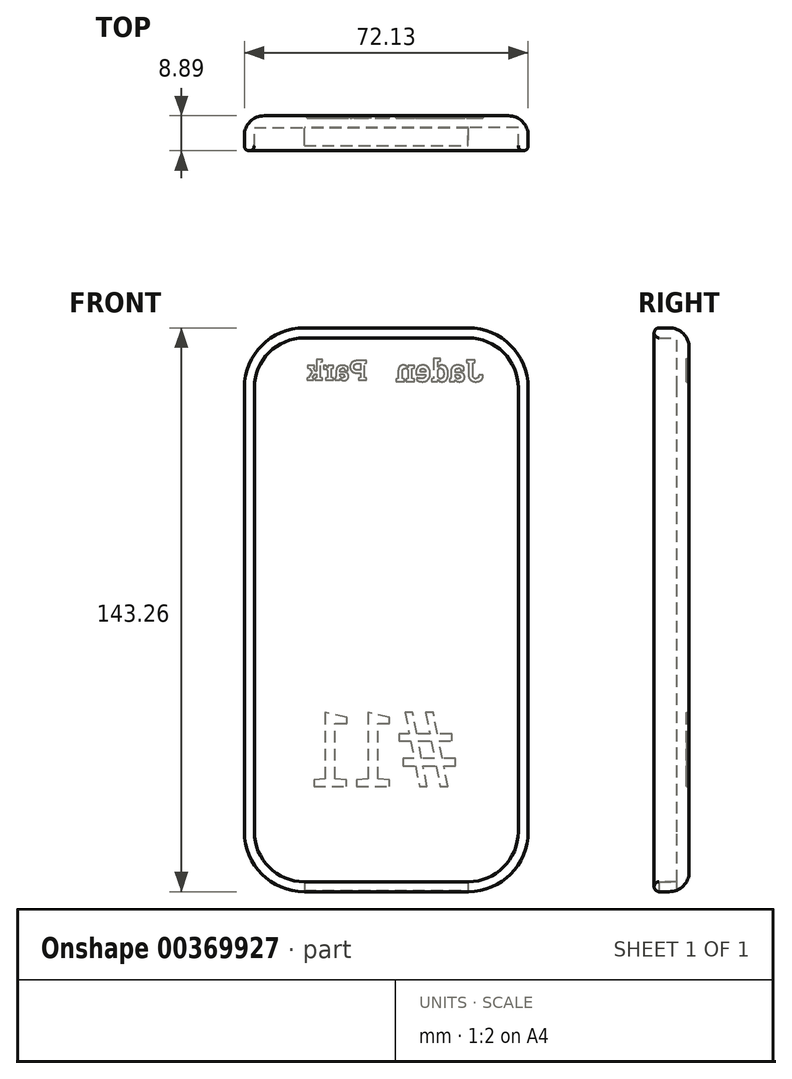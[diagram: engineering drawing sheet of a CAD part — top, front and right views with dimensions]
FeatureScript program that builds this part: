
annotation { "Feature Type Name" : "Feature", "Feature Type Description" : "" }
export const myFeature = defineFeature(function(context is Context, id is Id, definition is map)
    precondition{}
    {
        {
            var Q0;
            Q0=qCreatedBy(makeId("Front.planeOp"),FACE);
            var sketch = newSketch(context, id + "F0", { "sketchPlane" : qUnion([Q0])});
            skLineSegment(sketch, "E0.bottom", {"start": v(-22.84, 81.8) * mm, "end": v(18.81, 81.8) * mm});
            skLineSegment(sketch, "E0.top", {"start": v(-22.84, -56.38) * mm, "end": v(18.81, -56.38) * mm});
            skLineSegment(sketch, "E0.left", {"start": v(-35.54, 69.1) * mm, "end": v(-35.54, -43.68) * mm});
            skLineSegment(sketch, "E0.right", {"start": v(31.51, 69.1) * mm, "end": v(31.51, -43.68) * mm});
            skPoint(sketch, "E1.visualSharp", {"position": v(-35.54, 81.8) * mm});
            skArc(sketch, "E1.filletArc", {"start": v(-22.84, 81.8) * mm, "mid": v(-31.82, 78.08) * mm, "end": v(-35.54, 69.1) * mm});
            skPoint(sketch, "E2.visualSharp", {"position": v(31.51, 81.8) * mm});
            skArc(sketch, "E2.filletArc", {"start": v(31.51, 69.1) * mm, "mid": v(27.8, 78.08) * mm, "end": v(18.81, 81.8) * mm});
            skPoint(sketch, "E3.visualSharp", {"position": v(31.51, -56.38) * mm});
            skArc(sketch, "E3.filletArc", {"start": v(18.81, -56.38) * mm, "mid": v(27.8, -52.66) * mm, "end": v(31.51, -43.68) * mm});
            skPoint(sketch, "E4.visualSharp", {"position": v(-35.54, -56.38) * mm});
            skArc(sketch, "E4.filletArc", {"start": v(-35.54, -43.68) * mm, "mid": v(-31.82, -52.66) * mm, "end": v(-22.84, -56.38) * mm});
            skLineSegment(sketch, "E5.0", {"start": v(-22.84, 84.34) * mm, "end": v(18.81, 84.34) * mm});
            skArc(sketch, "E6.0", {"start": v(34.05, 69.1) * mm, "mid": v(29.6, 79.88) * mm, "end": v(18.81, 84.34) * mm});
            skArc(sketch, "E7.2", {"start": v(-22.84, 84.34) * mm, "mid": v(-33.62, 79.88) * mm, "end": v(-38.08, 69.1) * mm});
            skLineSegment(sketch, "E7.3", {"start": v(34.05, 69.1) * mm, "end": v(34.05, -43.68) * mm});
            skLineSegment(sketch, "E7.4", {"start": v(-38.08, 69.1) * mm, "end": v(-38.08, -43.68) * mm});
            skArc(sketch, "E7.5", {"start": v(-38.08, -43.68) * mm, "mid": v(-33.62, -54.45) * mm, "end": v(-22.84, -58.92) * mm});
            skLineSegment(sketch, "E7.6", {"start": v(-22.84, -58.92) * mm, "end": v(18.81, -58.92) * mm});
            skArc(sketch, "E7.7", {"start": v(18.81, -58.92) * mm, "mid": v(29.6, -54.45) * mm, "end": v(34.05, -43.68) * mm});
            skSolve(sketch);
        }
        {
            var Q0;
            Q0 = qSketchRegion(id + "F0", true);
            var Q1;
            Q1=makeQuery(id+"F0.imprint","IMPRINT",FACE,{"disambiguationData":[TD([[makeQuery(id+"F0.imprint","IMPRINT",EDGE,{"derivedFrom":sQuery(id+"F0.wireOp",EDGE,"E0.bottom")}),-1.0]])]});
            extrude(context, id + "F1", {"entities" : qUnion([Q0, Q1]), "depth" : 3.05 * mm});
        }
        {
            var Q0;
            Q0=makeQuery(id+"F0.imprint","IMPRINT",FACE,{"disambiguationData":[TD([[makeQuery(id+"F0.imprint","IMPRINT",EDGE,{"derivedFrom":sQuery(id+"F0.wireOp",EDGE,"E0.bottom")}),1.0]])]});
            extrude(context, id + "F2", {"entities" : qUnion([Q0]), "operationType" : NewBodyOperationType.ADD, "depth" : 8.9 * mm});
        }
        {
            var Q0;
            Q0=makeQuery(id+"F2.opExtrude","CAP_EDGE",EDGE,{"disambiguationData":[OSD([sQuery(id+"F0.wireOp",EDGE,"E1.filletArc")])],"isStart":false});
            var Q1;
            Q1=makeQuery(id+"F2.opExtrude","CAP_EDGE",EDGE,{"disambiguationData":[OSD([sQuery(id+"F0.wireOp",EDGE,"E0.bottom")])],"isStart":false});
            var Q2;
            Q2=makeQuery(id+"F2.opExtrude","CAP_EDGE",EDGE,{"disambiguationData":[OSD([sQuery(id+"F0.wireOp",EDGE,"E2.filletArc")])],"isStart":false});
            var Q3;
            Q3=makeQuery(id+"F2.opExtrude","CAP_EDGE",EDGE,{"disambiguationData":[OSD([sQuery(id+"F0.wireOp",EDGE,"E0.right")])],"isStart":false});
            var Q4;
            Q4=makeQuery(id+"F2.opExtrude","CAP_EDGE",EDGE,{"disambiguationData":[OSD([sQuery(id+"F0.wireOp",EDGE,"E3.filletArc")])],"isStart":false});
            var Q5;
            Q5=makeQuery(id+"F2.opExtrude","CAP_EDGE",EDGE,{"disambiguationData":[OSD([sQuery(id+"F0.wireOp",EDGE,"E4.filletArc")])],"isStart":false});
            var Q6;
            Q6=makeQuery(id+"F2.opExtrude","CAP_EDGE",EDGE,{"disambiguationData":[OSD([sQuery(id+"F0.wireOp",EDGE,"E7.3")])],"isStart":false});
            var Q7;
            Q7=makeQuery(id+"F2.opExtrude","CAP_EDGE",EDGE,{"disambiguationData":[OSD([sQuery(id+"F0.wireOp",EDGE,"E6.0")])],"isStart":false});
            var Q8;
            Q8=makeQuery(id+"F2.opExtrude","CAP_EDGE",EDGE,{"disambiguationData":[OSD([sQuery(id+"F0.wireOp",EDGE,"E5.0")])],"isStart":false});
            var Q9;
            Q9=makeQuery(id+"F2.opExtrude","CAP_EDGE",EDGE,{"disambiguationData":[OSD([sQuery(id+"F0.wireOp",EDGE,"E7.2")])],"isStart":false});
            var Q10;
            Q10=makeQuery(id+"F2.opExtrude","CAP_EDGE",EDGE,{"disambiguationData":[OSD([sQuery(id+"F0.wireOp",EDGE,"E7.5")])],"isStart":false});
            var Q11;
            Q11=makeQuery(id+"F2.opExtrude","CAP_EDGE",EDGE,{"disambiguationData":[OSD([sQuery(id+"F0.wireOp",EDGE,"E7.7")])],"isStart":false});
            var Q12;
            Q12=makeQuery(id+"F2.opExtrude","CAP_EDGE",EDGE,{"disambiguationData":[OSD([sQuery(id+"F0.wireOp",EDGE,"E0.left")])],"isStart":false});
            var Q13;
            Q13=makeQuery(id+"F2.opExtrude","CAP_EDGE",EDGE,{"disambiguationData":[OSD([sQuery(id+"F0.wireOp",EDGE,"E7.4")])],"isStart":false});
            fillet(context, id + "F3", {"entities" : qUnion([Q0, Q1, Q2, Q3, Q4, Q5, Q6, Q7, Q8, Q9, Q10, Q11, Q12, Q13]), "radius" : 1.27 * mm, "tangentPropagation" : true, "allowEdgeOverflow" : false});
        }
        {
            var Q0;
            Q0=makeQuery(id+"F1.opExtrude","CAP_EDGE",EDGE,{"disambiguationData":[OSD([sQuery(id+"F0.wireOp",EDGE,"E7.3")])],"isStart":true});
            fillet(context, id + "F4", {"entities" : qUnion([Q0]), "radius" : 5.08 * mm, "tangentPropagation" : true, "allowEdgeOverflow" : false});
        }
        {
            var Q0;
            {var subQ0=sQuery(id+"F0.wireOp",EDGE,"E7.6");Q0=makeQuery(id+"F2.boolean.opBoolean","MERGE",FACE,{"derivedFrom":[makeQuery(id+"F1.opExtrude","SWEPT_FACE",FACE,{"disambiguationData":[OSD([subQ0])]}),makeQuery(id+"F2.opExtrude","SWEPT_FACE",FACE,{"disambiguationData":[OSD([subQ0])]})]});}
            var sketch = newSketch(context, id + "F5", { "sketchPlane" : qUnion([Q0])});
            skLineSegment(sketch, "E8.bottom", {"start": v(-22.84, 7.62) * mm, "end": v(18.79, 7.62) * mm});
            skLineSegment(sketch, "E8.top", {"start": v(-22.84, 3.17) * mm, "end": v(18.79, 3.17) * mm});
            skLineSegment(sketch, "E8.left", {"start": v(-22.84, 7.62) * mm, "end": v(-22.84, 3.17) * mm});
            skLineSegment(sketch, "E8.right", {"start": v(18.79, 7.62) * mm, "end": v(18.79, 3.17) * mm});
            skSolve(sketch);
        }
        {
            var Q0;
            {var subQ0=sQuery(id+"F5.wireOp",EDGE,"E8.bottom");Q0=makeQuery(id+"F5.imprint","IMPRINT",FACE,{"disambiguationData":[TD([[makeQuery(id+"F5.imprint","IMPRINT",EDGE,{"derivedFrom":subQ0}),1.0]])]});}
            var Q1;
            {var subQ0=sQuery(id+"F5.wireOp",EDGE,"E8.top");Q1=makeQuery(id+"F5.imprint","IMPRINT",FACE,{"disambiguationData":[TD([[makeQuery(id+"F5.imprint","IMPRINT",EDGE,{"derivedFrom":subQ0}),1.0]])]});}
            extrude(context, id + "F6", {"entities" : qUnion([Q0, Q1]), "operationType" : NewBodyOperationType.REMOVE, "oppositeDirection" : true, "depth" : 12.7 * mm});
        }
        {
            var Q0;
            Q0=makeQuery(id+"F1.opExtrude","CAP_FACE",FACE,{"disambiguationData":[OSD([sQuery(id+"F0.wireOp",EDGE,"E5.0"),sQuery(id+"F0.wireOp",EDGE,"E6.0"),sQuery(id+"F0.wireOp",EDGE,"E7.2"),sQuery(id+"F0.wireOp",EDGE,"E7.3"),sQuery(id+"F0.wireOp",EDGE,"E7.4"),sQuery(id+"F0.wireOp",EDGE,"E7.5"),sQuery(id+"F0.wireOp",EDGE,"E7.6"),sQuery(id+"F0.wireOp",EDGE,"E7.7")])],"isStart":true});
            var sketch = newSketch(context, id + "F7", { "sketchPlane" : qUnion([Q0])});
            skText(sketch, "E9", { "text": "Jaden", "fontName": "RobotoSlab-Bold.ttf"});
            skPoint(sketch, "E9.firstSnap0", {"position": v(-26, 76.28) * mm});
            skText(sketch, "E10", { "text": "Park", "fontName": "RobotoSlab-Bold.ttf"});
            skText(sketch, "E11", { "text": "#11", "fontName": "RobotoSlab-Regular.ttf"});
            const initialGuessF7  = {"E9": [-0.0227, 0.07072, 1, 0, 0.00556], "E10": [0.00683, 0.07106, 1, 0, 0.00501], "E11": [-0.01644, -0.03219, 1, 0, 0.01902]};
            skSetInitialGuess(sketch, initialGuessF7);
            skSolve(sketch);
        }
        {
            var Q0;
            Q0=makeQuery(id+"F7.imprint","IMPRINT",FACE,{"disambiguationData":[TD([[makeQuery(id+"F7.imprint","IMPRINT",EDGE,{"derivedFrom":sQuery(id+"F7.wireOp",EDGE,"E11.sketch_text.stroke-0")}),-1.0]])]});
            var Q1;
            Q1=makeQuery(id+"F7.imprint","IMPRINT",FACE,{"disambiguationData":[TD([[makeQuery(id+"F7.imprint","IMPRINT",EDGE,{"derivedFrom":sQuery(id+"F7.wireOp",EDGE,"E11.sketch_text.stroke-32")}),-1.0]])]});
            var Q2;
            Q2=makeQuery(id+"F7.imprint","IMPRINT",FACE,{"disambiguationData":[TD([[makeQuery(id+"F7.imprint","IMPRINT",EDGE,{"derivedFrom":sQuery(id+"F7.wireOp",EDGE,"E11.sketch_text.stroke-42")}),-1.0]])]});
            var Q3;
            Q3=makeQuery(id+"F7.imprint","IMPRINT",FACE,{"disambiguationData":[TD([[makeQuery(id+"F7.imprint","IMPRINT",EDGE,{"derivedFrom":sQuery(id+"F7.wireOp",EDGE,"E9.sketch_text.stroke-0")}),-1.0]])]});
            var Q4;
            Q4=makeQuery(id+"F7.imprint","IMPRINT",FACE,{"disambiguationData":[TD([[makeQuery(id+"F7.imprint","IMPRINT",EDGE,{"derivedFrom":sQuery(id+"F7.wireOp",EDGE,"E9.sketch_text.stroke-18")}),-1.0]])]});
            var Q5;
            Q5=makeQuery(id+"F7.imprint","IMPRINT",FACE,{"disambiguationData":[TD([[makeQuery(id+"F7.imprint","IMPRINT",EDGE,{"derivedFrom":sQuery(id+"F7.wireOp",EDGE,"E9.sketch_text.stroke-53")}),-1.0]])]});
            var Q6;
            Q6=makeQuery(id+"F7.imprint","IMPRINT",FACE,{"disambiguationData":[TD([[makeQuery(id+"F7.imprint","IMPRINT",EDGE,{"derivedFrom":sQuery(id+"F7.wireOp",EDGE,"E9.sketch_text.stroke-82")}),-1.0]])]});
            var Q7;
            Q7=makeQuery(id+"F7.imprint","IMPRINT",FACE,{"disambiguationData":[TD([[makeQuery(id+"F7.imprint","IMPRINT",EDGE,{"derivedFrom":sQuery(id+"F7.wireOp",EDGE,"E9.sketch_text.stroke-106")}),-1.0]])]});
            var Q8;
            Q8=makeQuery(id+"F7.imprint","IMPRINT",FACE,{"disambiguationData":[TD([[makeQuery(id+"F7.imprint","IMPRINT",EDGE,{"derivedFrom":sQuery(id+"F7.wireOp",EDGE,"E10.sketch_text.stroke-0")}),-1.0]])]});
            var Q9;
            Q9=makeQuery(id+"F7.imprint","IMPRINT",FACE,{"disambiguationData":[TD([[makeQuery(id+"F7.imprint","IMPRINT",EDGE,{"derivedFrom":sQuery(id+"F7.wireOp",EDGE,"E10.sketch_text.stroke-23")}),-1.0]])]});
            var Q10;
            Q10=makeQuery(id+"F7.imprint","IMPRINT",FACE,{"disambiguationData":[TD([[makeQuery(id+"F7.imprint","IMPRINT",EDGE,{"derivedFrom":sQuery(id+"F7.wireOp",EDGE,"E10.sketch_text.stroke-58")}),-1.0]])]});
            var Q11;
            Q11=makeQuery(id+"F7.imprint","IMPRINT",FACE,{"disambiguationData":[TD([[makeQuery(id+"F7.imprint","IMPRINT",EDGE,{"derivedFrom":sQuery(id+"F7.wireOp",EDGE,"E10.sketch_text.stroke-77")}),-1.0]])]});
            extrude(context, id + "F8", {"entities" : qUnion([Q0, Q1, Q2, Q3, Q4, Q5, Q6, Q7, Q8, Q9, Q10, Q11]), "operationType" : NewBodyOperationType.REMOVE, "oppositeDirection" : true, "depth" : 0.64 * mm});
        }
    });
